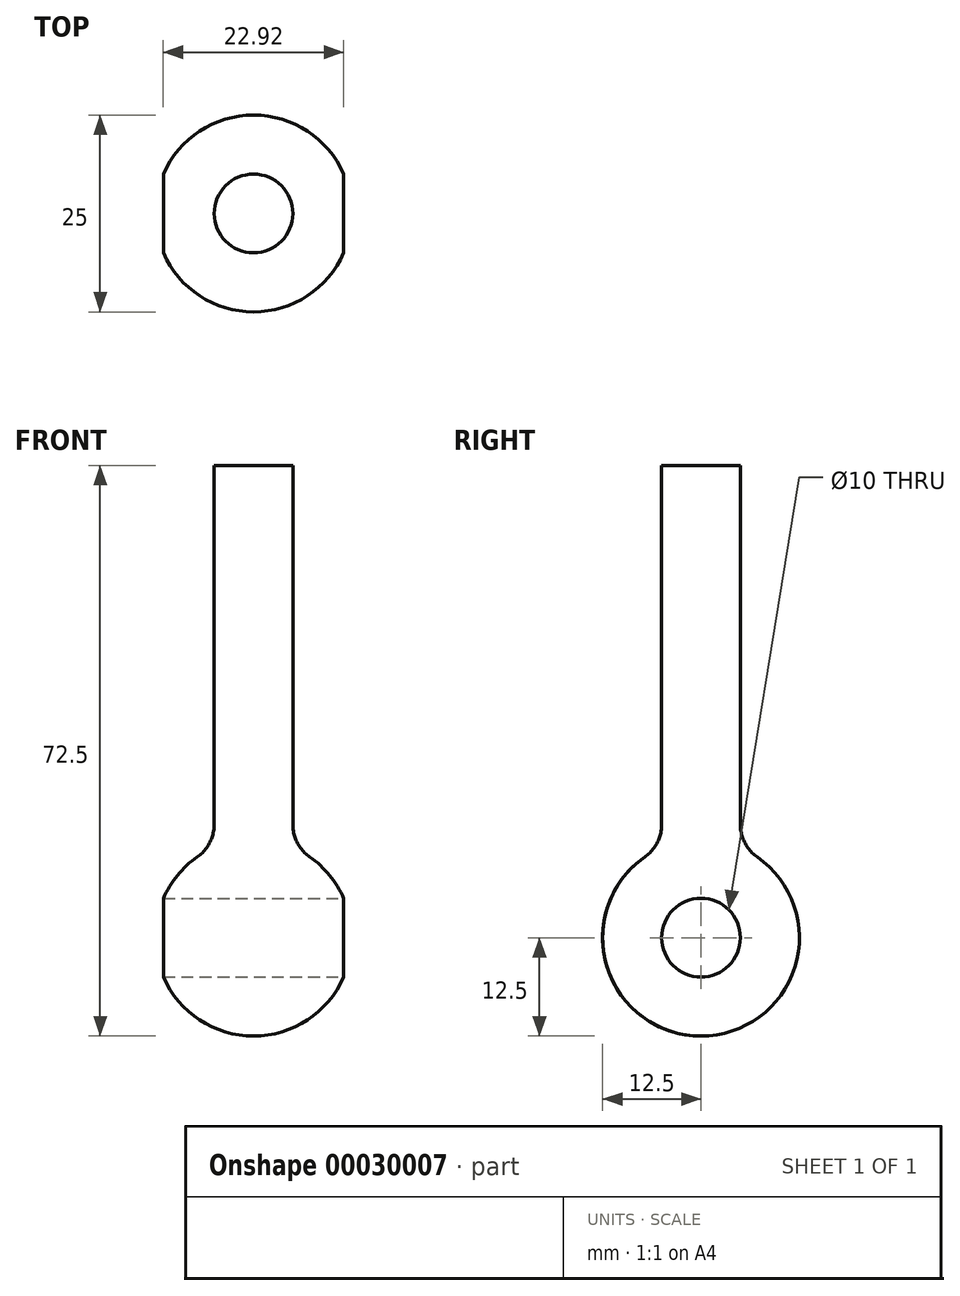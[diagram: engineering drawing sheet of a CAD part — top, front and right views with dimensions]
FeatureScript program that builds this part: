
annotation { "Feature Type Name" : "Feature", "Feature Type Description" : "" }
export const myFeature = defineFeature(function(context is Context, id is Id, definition is map)
    precondition{}
    {
        {
            var Q0;
            Q0=qCreatedBy(makeId("Right.planeOp"),FACE);
            var sketch = newSketch(context, id + "F0", { "sketchPlane" : qUnion([Q0])});
            skArc(sketch, "E0", {"start": v(0, -12.5) * mm, "mid": v(12.5, 0) * mm, "end": v(0, 12.5) * mm});
            skLineSegment(sketch, "E1", {"start": v(0, 24.21) * mm, "end": v(0, -26.63) * mm});
            skSolve(sketch);
        }
        {
            var Q0;
            {var subQ1=sQuery(id+"F0.wireOp",EDGE,"E0");Q0=makeQuery(id+"F0.imprint","IMPRINT",FACE,{"disambiguationData":[TD([[makeQuery(id+"F0.imprint","IMPRINT",EDGE,{"derivedFrom":subQ1}),1.0]])]});}
            var Q1;
            Q1=sQuery(id+"F0.wireOp",EDGE,"E1");
            revolve(context, id + "F1", {"entities" : qUnion([Q0]), "axis" : qUnion([Q1]), "revolveType" : RevolveType.FULL});
        }
        {
            var Q0;
            Q0=qCreatedBy(makeId("Right.planeOp"),FACE);
            var sketch = newSketch(context, id + "F2", { "sketchPlane" : qUnion([Q0])});
            skCircle(sketch, "E2", {"center": v(0, 0) * mm, "radius": 5 * mm});
            skSolve(sketch);
        }
        {
            var Q0;
            Q0=qCreatedBy(makeId("Top.planeOp"),FACE);
            var sketch = newSketch(context, id + "F3", { "sketchPlane" : qUnion([Q0])});
            skCircle(sketch, "E3", {"center": v(0, 0) * mm, "radius": 5 * mm});
            skSolve(sketch);
        }
        {
            var Q0;
            Q0 = qSketchRegion(id + "F3", true);
            extrude(context, id + "F4", {"entities" : qUnion([Q0]), "operationType" : NewBodyOperationType.ADD, "depth" : 60 * mm});
        }
        {
            var Q0;
            Q0 = qSketchRegion(id + "F2", true);
            var Q1;
            Q1=makeQuery(id+"F1.opRevolve","SWEPT_BODY",BODY,{"disambiguationData":[OSD([sQuery(id+"F0.wireOp",EDGE,"E0"),sQuery(id+"F0.wireOp",EDGE,"E1")])]});
            var Q2;
            Q2=makeQuery(id+"F1.opRevolve","SWEPT_BODY",BODY,{"disambiguationData":[OSD([sQuery(id+"F0.wireOp",EDGE,"E0"),sQuery(id+"F0.wireOp",EDGE,"E1")])]});
            extrude(context, id + "F5", {"entities" : qUnion([Q0]), "operationType" : NewBodyOperationType.REMOVE, "endBound" : BoundingType.SYMMETRIC, "oppositeDirection" : true, "endBoundEntityBody" : qUnion([Q1]), "depth" : 30000 * mm, "hasSecondDirection" : true, "secondDirectionBound" : SecondDirectionBoundingType.UP_TO_BODY, "secondDirectionOppositeDirection" : true, "secondDirectionBoundEntityBody" : qUnion([Q2]), "secondDirectionDepth" : 25 * mm});
        }
        {
            var Q0;
            Q0=makeQuery(id+"F4.boolean.opBoolean","INTERSECT",EDGE,{"derivedFrom":[makeQuery(id+"F1.opRevolve","SWEPT_FACE",FACE,{"disambiguationData":[OSD([sQuery(id+"F0.wireOp",EDGE,"E0")])]}),makeQuery(id+"F4.opExtrude","SWEPT_FACE",FACE,{"disambiguationData":[OSD([sQuery(id+"F3.wireOp",EDGE,"E3")])]})]});
            fillet(context, id + "F6", {"entities" : qUnion([Q0]), "radius" : 5 * mm, "tangentPropagation" : true, "allowEdgeOverflow" : false});
        }
    });
